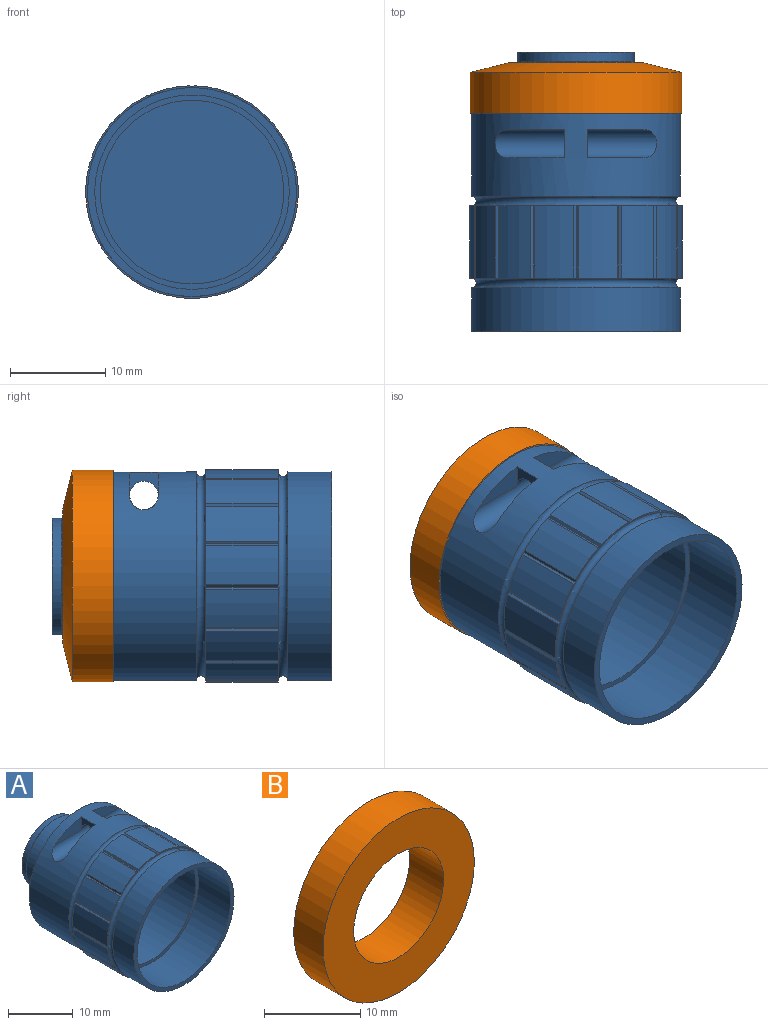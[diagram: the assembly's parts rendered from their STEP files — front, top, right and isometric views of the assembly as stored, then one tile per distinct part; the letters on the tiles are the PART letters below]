
ASSEMBLY  parts=2 mates=1
PART A: 96 faces, bbox 24.5x29.3x24.5 mm
  f0: cylinder r=1.5mm len=16.93mm, axis (-1,0,0), area 86.4mm2, adj f1,f90,f91,f92,f93,f94,f95
  f1: cylinder r=10.95mm len=21.9mm, axis (0,-1,0), area 550.3mm2, adj f0,f47,f59,f90,f91,f92,f93,f94
  f2: plane 4.45x1.14mm, normal (0,1,0), area 0.9mm2, adj f17,f47,f87,f88
  f3: plane 3.68x2.76mm, normal (0,1,0), area 0.9mm2, adj f18,f47,f85,f86
  f4: plane 3.94x2.39mm, normal (0,1,0), area 0.9mm2, adj f19,f47,f83,f84
  f5: plane 4.53x0.74mm, normal (0,1,0), area 0.9mm2, adj f20,f47,f81,f82
  f6: plane 4.33x1.58mm, normal (0,1,0), area 0.9mm2, adj f21,f47,f79,f80
  f7: plane 3.4x3.09mm, normal (0,1,0), area 0.9mm2, adj f22,f47,f77,f78
  f8: plane 4.16x1.99mm, normal (0,1,0), area 0.9mm2, adj f23,f47,f75,f76
  f9: plane 4.55x0.44mm, normal (0,1,0), area 0.9mm2, adj f24,f47,f73,f74
  f10: plane 4.16x1.99mm, normal (0,1,0), area 0.9mm2, adj f25,f47,f71,f72
  f11: plane 3.4x3.09mm, normal (0,1,0), area 0.9mm2, adj f26,f47,f69,f70
  f12: plane 4.33x1.58mm, normal (0,1,0), area 0.9mm2, adj f27,f47,f67,f68
  f13: plane 4.53x0.74mm, normal (0,1,0), area 0.9mm2, adj f28,f47,f65,f66
  f14: plane 3.94x2.39mm, normal (0,1,0), area 0.9mm2, adj f29,f47,f63,f64
  f15: plane 3.68x2.76mm, normal (0,1,0), area 0.9mm2, adj f30,f47,f61,f62
  f16: plane 4.45x1.14mm, normal (0,1,0), area 0.9mm2, adj f31,f47,f60,f89
  f17: cylinder r=11.15mm len=7.6mm, axis (0,-1,0), area 31.7mm2, adj f2,f32,f87,f88
  f18: cylinder r=11.15mm len=7.6mm, axis (0,-1,0), area 31.7mm2, adj f3,f33,f85,f86
  f19: cylinder r=11.15mm len=7.6mm, axis (0,-1,0), area 31.7mm2, adj f4,f34,f83,f84
  f20: cylinder r=11.15mm len=7.6mm, axis (0,-1,0), area 31.7mm2, adj f5,f35,f81,f82
  f21: cylinder r=11.15mm len=7.6mm, axis (0,-1,0), area 31.7mm2, adj f6,f36,f79,f80
  f22: cylinder r=11.15mm len=7.6mm, axis (0,-1,0), area 31.7mm2, adj f7,f37,f77,f78
  f23: cylinder r=11.15mm len=7.6mm, axis (0,-1,0), area 31.7mm2, adj f8,f38,f75,f76
  f24: cylinder r=11.15mm len=7.6mm, axis (0,-1,0), area 31.7mm2, adj f9,f39,f73,f74
  f25: cylinder r=11.15mm len=7.6mm, axis (0,-1,0), area 31.7mm2, adj f10,f40,f71,f72
  f26: cylinder r=11.15mm len=7.6mm, axis (0,-1,0), area 31.7mm2, adj f11,f41,f69,f70
  f27: cylinder r=11.15mm len=7.6mm, axis (0,-1,0), area 31.7mm2, adj f12,f42,f67,f68
  f28: cylinder r=11.15mm len=7.6mm, axis (0,-1,0), area 31.7mm2, adj f13,f43,f65,f66
  f29: cylinder r=11.15mm len=7.6mm, axis (0,-1,0), area 31.7mm2, adj f14,f44,f63,f64
  f30: cylinder r=11.15mm len=7.6mm, axis (0,-1,0), area 31.7mm2, adj f15,f45,f61,f62
  f31: cylinder r=11.15mm len=7.6mm, axis (0,-1,0), area 31.7mm2, adj f16,f46,f60,f89
  f32: plane 4.45x1.14mm, normal (0,-1,0), area 0.9mm2, adj f17,f48,f87,f88
  f33: plane 3.68x2.76mm, normal (0,-1,0), area 0.9mm2, adj f18,f48,f85,f86
  f34: plane 3.94x2.39mm, normal (0,-1,0), area 0.9mm2, adj f19,f48,f83,f84
  f35: plane 4.53x0.74mm, normal (0,-1,0), area 0.9mm2, adj f20,f48,f81,f82
  f36: plane 4.33x1.58mm, normal (0,-1,0), area 0.9mm2, adj f21,f48,f79,f80
  f37: plane 3.4x3.09mm, normal (0,-1,0), area 0.9mm2, adj f22,f48,f77,f78
  f38: plane 4.16x1.99mm, normal (0,-1,0), area 0.9mm2, adj f23,f48,f75,f76
  f39: plane 4.55x0.44mm, normal (0,-1,0), area 0.9mm2, adj f24,f48,f73,f74
  f40: plane 4.16x1.99mm, normal (0,-1,0), area 0.9mm2, adj f25,f48,f71,f72
  f41: plane 3.4x3.09mm, normal (0,-1,0), area 0.9mm2, adj f26,f48,f69,f70
  f42: plane 4.33x1.58mm, normal (0,-1,0), area 0.9mm2, adj f27,f48,f67,f68
  f43: plane 4.53x0.74mm, normal (0,-1,0), area 0.9mm2, adj f28,f48,f65,f66
  f44: plane 3.94x2.39mm, normal (0,-1,0), area 0.9mm2, adj f29,f48,f63,f64
  f45: plane 3.68x2.76mm, normal (0,-1,0), area 0.9mm2, adj f30,f48,f61,f62
  f46: plane 4.45x1.14mm, normal (0,-1,0), area 0.9mm2, adj f31,f48,f60,f89
  f47: torus R=10.95mm, axis (0,-1,0), area 104.9mm2, adj f1,f2,f3,f4,f5,f6,f7,f8
  f48: torus R=10.95mm, axis (0,-1,0), area 104.9mm2, adj f32,f33,f34,f35,f36,f37,f38,f39
  f49: cylinder r=10.95mm len=21.9mm, axis (0,-1,0), area 316.5mm2, adj f48,f50
  f50: plane 21.9x21.9mm, normal (0,-1,0), area 49.8mm2, adj f49,f51
  f51: cylinder r=10.2mm len=20.4mm, axis (0,-1,0), area 448.6mm2, adj f50,f52
  f52: plane 20.4x20.4mm, normal (0,-1,0), area 35.8mm2, adj f51,f53
  f53: cylinder r=9.62mm len=19.25mm, axis (0,-1,0), area 586.6mm2, adj f52,f54
  f54: plane 19.25x19.25mm, normal (0,-1,0), area 291mm2, adj f53
  f55: plane 12.2x12.2mm, normal (0,1,0), area 116.9mm2, adj f56
  f56: cylinder r=6.1mm len=12.2mm, axis (0,-1,0), area 38.3mm2, adj f55,f57
  f57: cone r=6.1mm half-angle=51.3deg, axis (0,-1,0), area 25.5mm2, adj f56,f58
  f58: cylinder r=6.6mm len=13.2mm, axis (0,-1,0), area 207.3mm2, adj f57,f59
  f59: plane 21.9x21.9mm, normal (0,1,0), area 239.8mm2, adj f1,f58
  f60: plane 7.6x0.28mm, normal (0.89,0,0.46), area 2.4mm2, adj f16,f31,f46,f61
  f61: plane 7.6x0.31mm, normal (-0.25,0,0.97), area 2.4mm2, adj f15,f30,f45,f60
  f62: plane 7.6x0.32mm, normal (1,0,0.06), area 2.4mm2, adj f15,f30,f45,f63
  f63: plane 7.6x0.31mm, normal (0.16,0,0.99), area 2.4mm2, adj f14,f29,f44,f62
  f64: plane 7.6x0.3mm, normal (0.94,0,-0.35), area 2.4mm2, adj f14,f29,f44,f65
  f65: plane 7.6x0.26mm, normal (0.55,0,0.84), area 2.4mm2, adj f13,f28,f43,f64
  f66: plane 7.6x0.22mm, normal (0.71,0,-0.7), area 2.4mm2, adj f13,f28,f43,f67
  f67: plane 7.6x0.27mm, normal (0.84,0,0.54), area 2.4mm2, adj f12,f27,f42,f66
  f68: plane 7.6x0.29mm, normal (0.36,0,-0.93), area 2.4mm2, adj f12,f27,f42,f69
  f69: plane 7.6x0.31mm, normal (0.99,0,0.15), area 2.4mm2, adj f11,f26,f41,f68
  f70: plane 7.6x0.32mm, normal (-0.05,0,-1), area 2.4mm2, adj f11,f26,f41,f71
  f71: plane 7.6x0.3mm, normal (0.96,0,-0.26), area 2.4mm2, adj f10,f25,f40,f70
  f72: plane 7.6x0.28mm, normal (-0.45,0,-0.89), area 2.4mm2, adj f10,f25,f40,f73
  f73: plane 7.6x0.24mm, normal (0.77,0,-0.63), area 2.4mm2, adj f9,f24,f39,f72
  f74: plane 7.6x0.24mm, normal (-0.77,0,-0.63), area 2.4mm2, adj f9,f24,f39,f75
  f75: plane 7.6x0.28mm, normal (0.45,0,-0.89), area 2.4mm2, adj f8,f23,f38,f74
  f76: plane 7.6x0.3mm, normal (-0.96,0,-0.26), area 2.4mm2, adj f8,f23,f38,f77
  f77: plane 7.6x0.32mm, normal (0.05,0,-1), area 2.4mm2, adj f7,f22,f37,f76
  f78: plane 7.6x0.31mm, normal (-0.99,0,0.15), area 2.4mm2, adj f7,f22,f37,f79
  f79: plane 7.6x0.29mm, normal (-0.36,0,-0.93), area 2.4mm2, adj f6,f21,f36,f78
  f80: plane 7.6x0.27mm, normal (-0.84,0,0.54), area 2.4mm2, adj f6,f21,f36,f81
  f81: plane 7.6x0.22mm, normal (-0.71,0,-0.7), area 2.4mm2, adj f5,f20,f35,f80
  f82: plane 7.6x0.26mm, normal (-0.55,0,0.84), area 2.4mm2, adj f5,f20,f35,f83
  f83: plane 7.6x0.3mm, normal (-0.94,0,-0.35), area 2.4mm2, adj f4,f19,f34,f82
  f84: plane 7.6x0.31mm, normal (-0.16,0,0.99), area 2.4mm2, adj f4,f19,f34,f85
  f85: plane 7.6x0.32mm, normal (-1,0,0.06), area 2.4mm2, adj f3,f18,f33,f84
  f86: plane 7.6x0.31mm, normal (0.25,0,0.97), area 2.4mm2, adj f3,f18,f33,f87
  f87: plane 7.6x0.28mm, normal (-0.89,0,0.46), area 2.4mm2, adj f2,f17,f32,f86
  f88: plane 7.6x0.25mm, normal (0.62,0,0.78), area 2.4mm2, adj f2,f17,f32,f89
  f89: plane 7.6x0.25mm, normal (-0.62,0,0.78), area 2.4mm2, adj f16,f31,f46,f88
  f90: plane 5.76x2.43mm, normal (0,1,0), area 8.9mm2, adj f0,f1,f91
  f91: plane 3x2.43mm, normal (-1,0,0), area 3.8mm2, adj f0,f1,f90,f92
  f92: plane 5.76x2.43mm, normal (0,-1,0), area 8.9mm2, adj f0,f1,f91
  f93: plane 3x2.43mm, normal (1,0,0), area 3.8mm2, adj f0,f1,f94,f95
  f94: plane 5.76x2.43mm, normal (0,1,0), area 8.9mm2, adj f0,f1,f93
  f95: plane 5.76x2.43mm, normal (0,-1,0), area 8.9mm2, adj f0,f1,f93
PART B: 5 faces, bbox 22.2x5.6x22.2 mm
  f0: cylinder r=11.1mm len=22.2mm, axis (0,-1,0), area 299.9mm2, adj f1,f4
  f1: plane 22.2x22.2mm, normal (0,-1,0), area 250.2mm2, adj f0,f2
  f2: cylinder r=6.6mm len=13.2mm, axis (0,-1,0), area 207.3mm2, adj f1,f3
  f3: torus R=6.53mm, axis (0,-1,0), area 24.1mm2, adj f2,f4
  f4: cone r=7.05mm half-angle=76.1deg, axis (0,-1,0), area 237.9mm2, adj f0,f3
PLACE A t=(25.34,19.22,12.14)mm
PLACE B t=(25.34,42.12,12.14)mm
MATE parallel B.f0 <-> A.f1  axis (0,-1,0) through (25.34,42.12,12.14)mm
